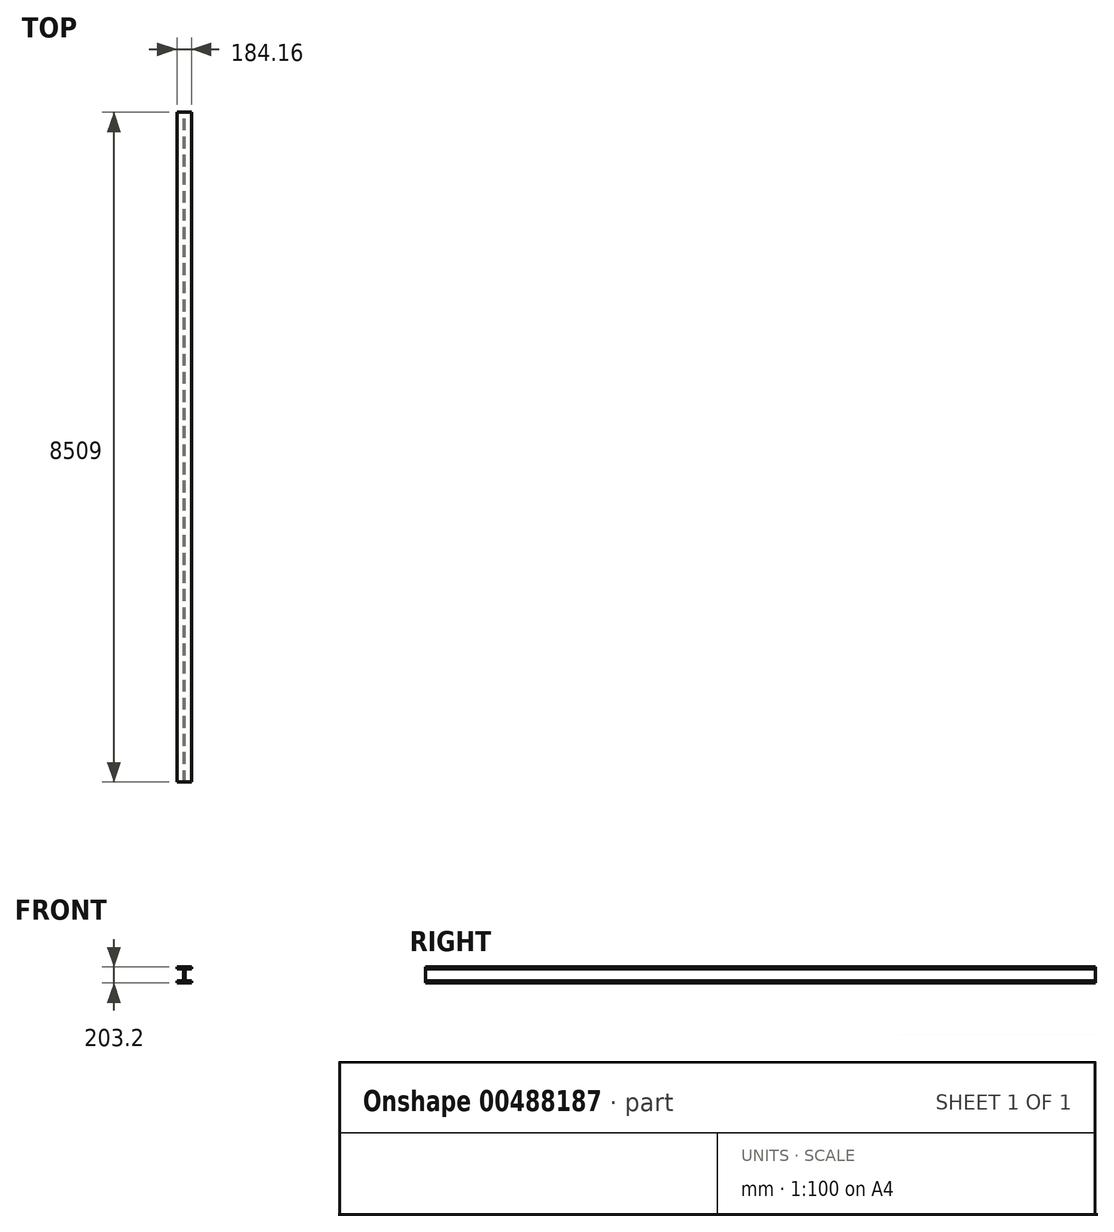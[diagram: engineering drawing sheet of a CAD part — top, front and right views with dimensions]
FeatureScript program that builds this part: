
annotation { "Feature Type Name" : "Feature", "Feature Type Description" : "" }
export const myFeature = defineFeature(function(context is Context, id is Id, definition is map)
    precondition{}
    {
        {
            var Q0;
            Q0=qCreatedBy(makeId("Front.planeOp"),FACE);
            var sketch = newSketch(context, id + "F0", { "sketchPlane" : qUnion([Q0])});
            skLineSegment(sketch, "E0", {"start": v(92.08, -76.2) * mm, "end": v(12.07, -76.2) * mm});
            skLineSegment(sketch, "E1", {"start": v(9.52, -73.66) * mm, "end": v(9.52, 73.66) * mm});
            skLineSegment(sketch, "E2", {"start": v(12.07, 76.2) * mm, "end": v(92.08, 76.2) * mm});
            skLineSegment(sketch, "E3", {"start": v(-92.08, 76.2) * mm, "end": v(-12.07, 76.2) * mm});
            skLineSegment(sketch, "E4", {"start": v(-9.53, 73.66) * mm, "end": v(-9.53, -73.66) * mm});
            skLineSegment(sketch, "E5", {"start": v(-12.06, -76.2) * mm, "end": v(-92.08, -76.2) * mm});
            skLineSegment(sketch, "E6", {"start": v(0, 0) * mm, "end": v(-9.52, 0) * mm, "construction": true});
            skLineSegment(sketch, "E7", {"start": v(0, 0) * mm, "end": v(9.52, 0) * mm, "construction": true});
            skLineSegment(sketch, "E8", {"start": v(0, 0) * mm, "end": v(0, 101.6) * mm, "construction": true});
            skLineSegment(sketch, "E9", {"start": v(0, 0) * mm, "end": v(0, -101.6) * mm, "construction": true});
            skPoint(sketch, "E10.visualSharp", {"position": v(-9.53, 76.2) * mm});
            skArc(sketch, "E10.filletArc", {"start": v(-9.52, 73.66) * mm, "mid": v(-10.27, 75.46) * mm, "end": v(-12.07, 76.2) * mm});
            skPoint(sketch, "E11.visualSharp", {"position": v(9.53, 76.2) * mm});
            skArc(sketch, "E11.filletArc", {"start": v(12.07, 76.2) * mm, "mid": v(10.27, 75.46) * mm, "end": v(9.52, 73.66) * mm});
            skPoint(sketch, "E12.visualSharp", {"position": v(9.53, -76.2) * mm});
            skArc(sketch, "E12.filletArc", {"start": v(9.52, -73.66) * mm, "mid": v(10.27, -75.46) * mm, "end": v(12.07, -76.2) * mm});
            skPoint(sketch, "E13.visualSharp", {"position": v(-9.53, -76.2) * mm});
            skArc(sketch, "E13.filletArc", {"start": v(-12.06, -76.2) * mm, "mid": v(-10.27, -75.46) * mm, "end": v(-9.52, -73.66) * mm});
            skPoint(sketch, "E14.visualSharp", {"position": v(-92.08, 101.6) * mm});
            skPoint(sketch, "E15.visualSharp", {"position": v(92.08, 101.6) * mm});
            skPoint(sketch, "E16.visualSharp", {"position": v(92.08, 76.2) * mm});
            skPoint(sketch, "E17.visualSharp", {"position": v(92.08, -101.6) * mm});
            skPoint(sketch, "E18.visualSharp", {"position": v(-92.08, -76.2) * mm});
            skPoint(sketch, "E19.visualSharp", {"position": v(-92.08, -101.6) * mm});
            skLineSegment(sketch, "E20", {"start": v(92.08, -76.2) * mm, "end": v(92.08, -101.6) * mm});
            skLineSegment(sketch, "E21", {"start": v(-92.08, -76.2) * mm, "end": v(-92.08, -101.6) * mm});
            skLineSegment(sketch, "E22", {"start": v(-92.08, 101.6) * mm, "end": v(-92.08, 76.2) * mm});
            skLineSegment(sketch, "E23", {"start": v(92.08, 101.6) * mm, "end": v(92.08, 76.2) * mm});
            skLineSegment(sketch, "E24", {"start": v(-92.08, 101.6) * mm, "end": v(92.08, 101.6) * mm});
            skLineSegment(sketch, "E25", {"start": v(-92.07, -101.6) * mm, "end": v(92.08, -101.6) * mm});
            skSolve(sketch);
        }
        {
            var Q0;
            Q0=makeQuery(id+"F0.imprint","IMPRINT",FACE,{"disambiguationData":[TD([[makeQuery(id+"F0.imprint","IMPRINT",EDGE,{"derivedFrom":sQuery(id+"F0.wireOp",EDGE,"E0")}),1.0]])]});
            extrude(context, id + "F1", {"entities" : qUnion([Q0]), "depth" : 8509 * mm, "offsetDistance" : 25.4 * mm});
        }
    });
